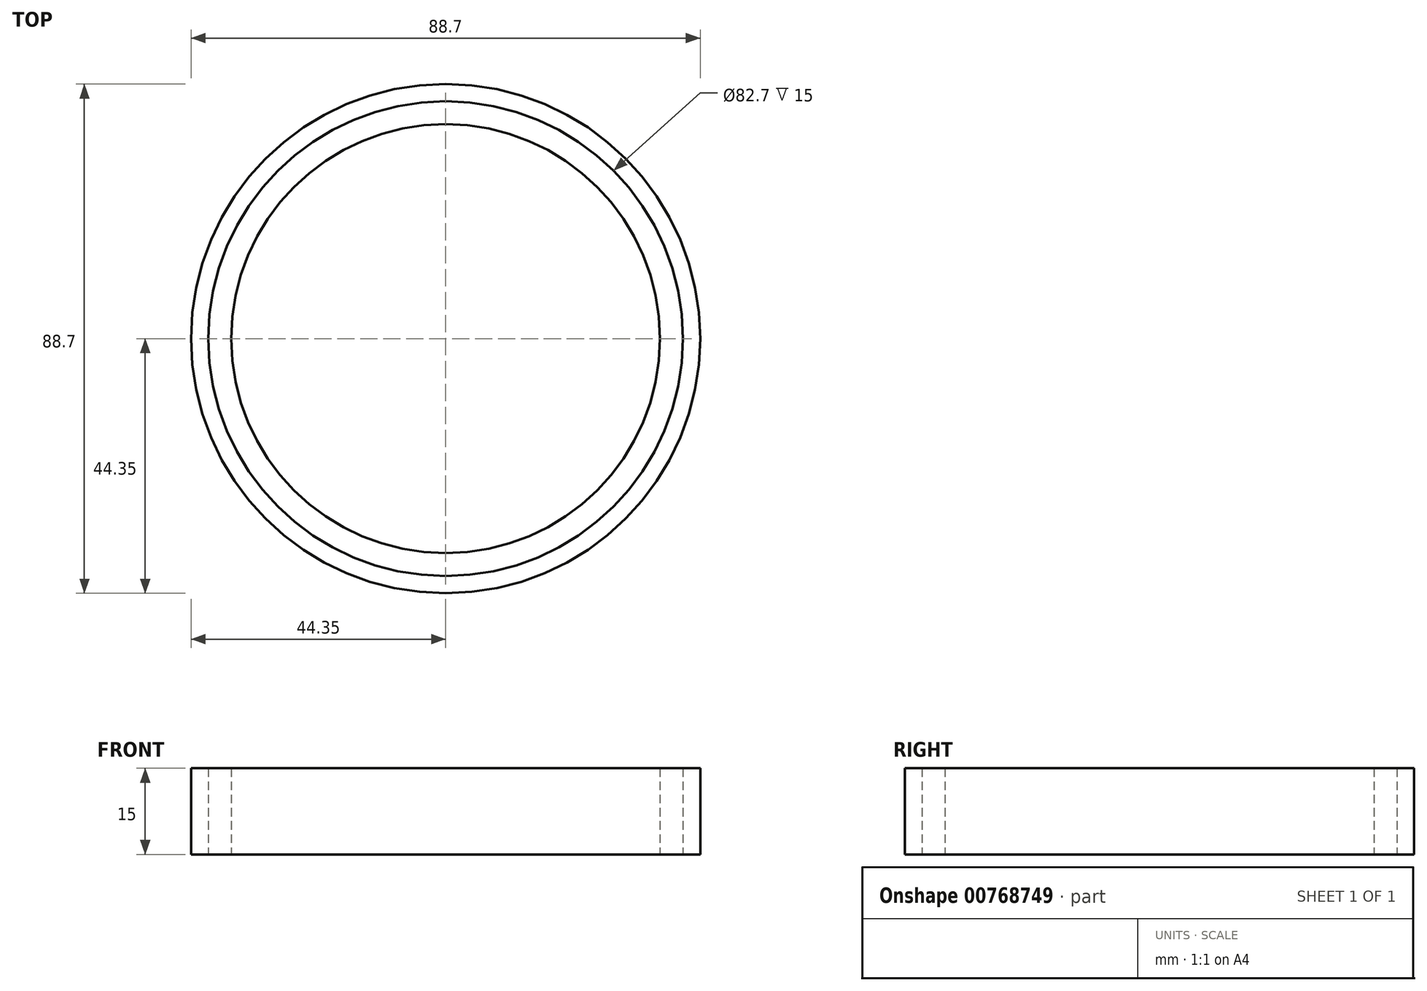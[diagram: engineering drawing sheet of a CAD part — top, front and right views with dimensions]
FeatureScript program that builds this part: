
annotation { "Feature Type Name" : "Feature", "Feature Type Description" : "" }
export const myFeature = defineFeature(function(context is Context, id is Id, definition is map)
    precondition{}
    {
        {
            var Q0;
            Q0=qCreatedBy(makeId("Top.planeOp"),FACE);
            var sketch = newSketch(context, id + "F0", { "sketchPlane" : qUnion([Q0])});
            skCircle(sketch, "E0", {"center": v(0, 0) * mm, "radius": 37.35 * mm});
            skCircle(sketch, "E1", {"center": v(0, 0) * mm, "radius": 40.85 * mm});
            skCircle(sketch, "E2", {"center": v(0, 0) * mm, "radius": 41.35 * mm});
            skCircle(sketch, "E3", {"center": v(0, 0) * mm, "radius": 44.35 * mm});
            skSolve(sketch);
        }
        {
            var Q0;
            Q0 = qSketchRegion(id + "F0", true);
            var Q1;
            Q1=makeQuery(id+"F0.imprint","IMPRINT",FACE,{"disambiguationData":[TD([[makeQuery(id+"F0.imprint","IMPRINT",EDGE,{"derivedFrom":sQuery(id+"F0.wireOp",EDGE,"E0")}),1.0]])]});
            extrude(context, id + "F1", {"entities" : qUnion([Q0, Q1]), "depth" : 15 * mm, "offsetDistance" : 25 * mm});
        }
    });
